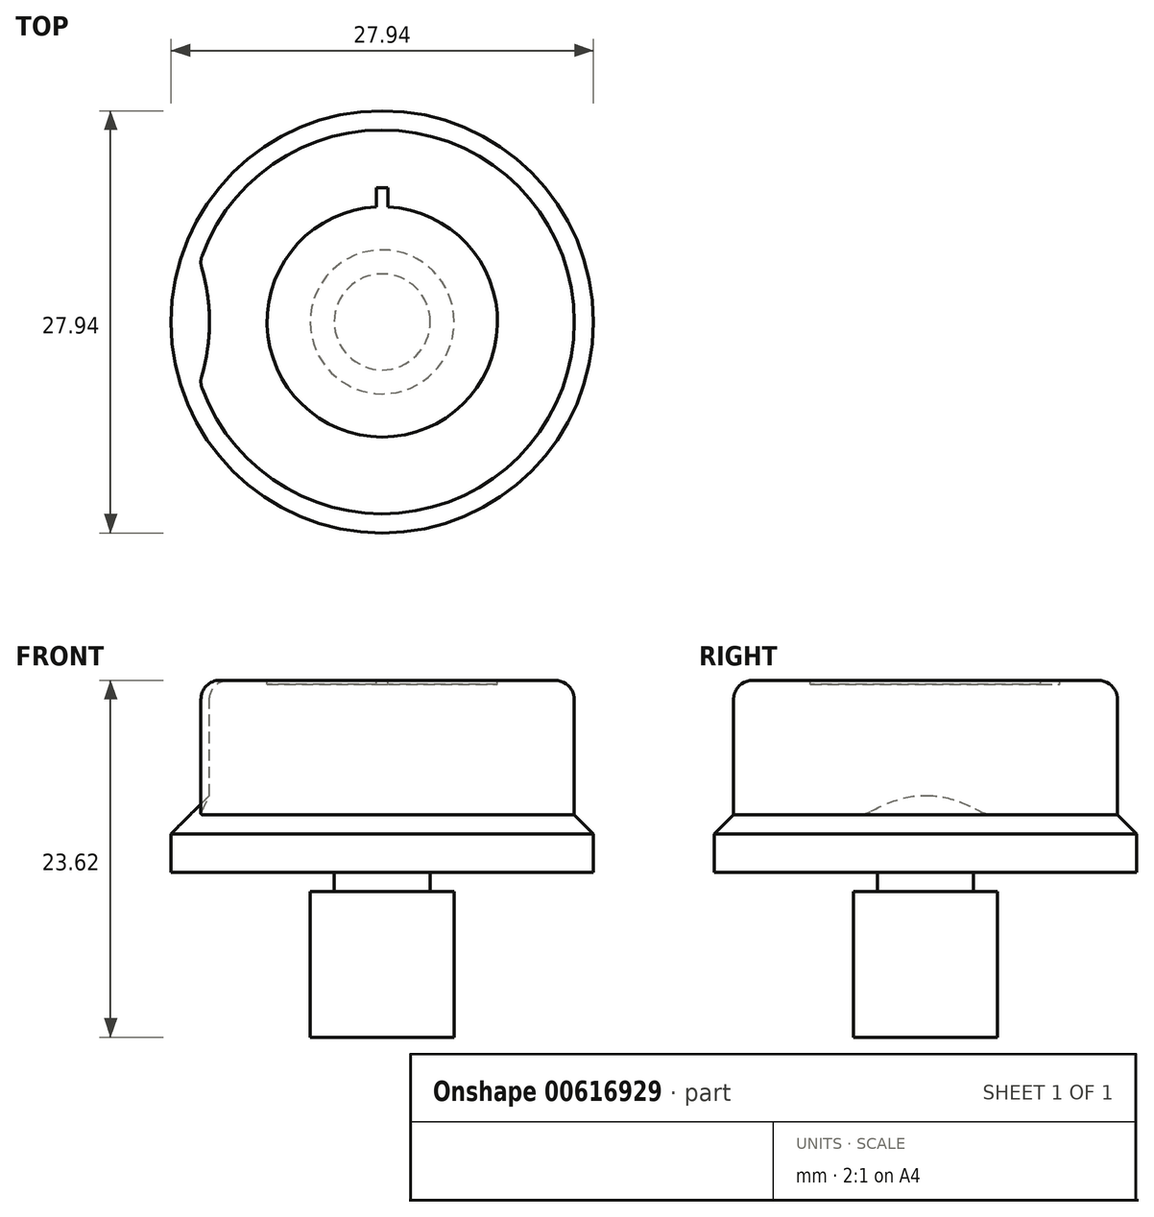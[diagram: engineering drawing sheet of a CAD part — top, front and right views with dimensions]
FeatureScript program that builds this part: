
annotation { "Feature Type Name" : "Feature", "Feature Type Description" : "" }
export const myFeature = defineFeature(function(context is Context, id is Id, definition is map)
    precondition{}
    {
        {
            var Q0;
            Q0=qCreatedBy(makeId("Front.planeOp"),FACE);
            var sketch = newSketch(context, id + "F0", { "sketchPlane" : qUnion([Q0])});
            skLineSegment(sketch, "E0", {"start": v(0, 0) * mm, "end": v(0, 23.62) * mm});
            skLineSegment(sketch, "E1", {"start": v(0, 23.62) * mm, "end": v(12.7, 23.62) * mm});
            skLineSegment(sketch, "E2", {"start": v(12.7, 23.62) * mm, "end": v(12.7, 14.73) * mm});
            skLineSegment(sketch, "E3", {"start": v(12.7, 14.73) * mm, "end": v(13.97, 13.46) * mm});
            skLineSegment(sketch, "E4", {"start": v(13.97, 13.46) * mm, "end": v(13.97, 10.92) * mm});
            skLineSegment(sketch, "E5", {"start": v(13.97, 10.92) * mm, "end": v(3.17, 10.92) * mm});
            skLineSegment(sketch, "E6", {"start": v(3.17, 10.92) * mm, "end": v(3.17, 9.65) * mm});
            skLineSegment(sketch, "E7", {"start": v(3.17, 9.65) * mm, "end": v(4.76, 9.65) * mm});
            skLineSegment(sketch, "E8", {"start": v(4.76, 9.65) * mm, "end": v(4.76, 0) * mm});
            skLineSegment(sketch, "E9", {"start": v(4.76, 0) * mm, "end": v(0, 0) * mm});
            skSolve(sketch);
        }
        {
            var Q0;
            Q0=makeQuery(id+"F0.imprint","IMPRINT",FACE,{"disambiguationData":[TD([[makeQuery(id+"F0.imprint","IMPRINT",EDGE,{"derivedFrom":sQuery(id+"F0.wireOp",EDGE,"E0")}),-1.0]])]});
            var Q1;
            Q1=sQuery(id+"F0.wireOp",EDGE,"E0");
            revolve(context, id + "F1", {"entities" : qUnion([Q0]), "axis" : qUnion([Q1]), "revolveType" : RevolveType.FULL});
        }
        {
            var Q0;
            Q0=makeQuery(id+"F1.opRevolve","SWEPT_FACE",FACE,{"disambiguationData":[OSD([sQuery(id+"F0.wireOp",EDGE,"E1")])]});
            var sketch = newSketch(context, id + "F2", { "sketchPlane" : qUnion([Q0])});
            skCircle(sketch, "E10", {"center": v(-24.13, 0) * mm, "radius": 12.7 * mm});
            skSolve(sketch);
        }
        {
            var Q0;
            Q0 = qSketchRegion(id + "F2", true);
            var Q1;
            Q1=makeQuery(id+"F1.opRevolve","SWEPT_FACE",FACE,{"disambiguationData":[OSD([sQuery(id+"F0.wireOp",EDGE,"E3")])]});
            extrude(context, id + "F3", {"entities" : qUnion([Q0]), "operationType" : NewBodyOperationType.REMOVE, "endBound" : BoundingType.UP_TO_SURFACE, "oppositeDirection" : true, "depth" : 25.4 * mm, "endBoundEntityFace" : qUnion([Q1]), "offsetDistance" : 25.4 * mm});
        }
        {
            var Q0;
            Q0=makeQuery(id+"F1.opRevolve","SWEPT_FACE",FACE,{"disambiguationData":[OSD([sQuery(id+"F0.wireOp",EDGE,"E1")])]});
            var Q1;
            {var subQ0=sQuery(id+"F2.wireOp",EDGE,"E10");var subQ4=makeQuery(id+"F3.boolean.opBoolean","COPY",FACE,{"derivedFrom":makeQuery(id+"F3.opExtrude","SWEPT_FACE",FACE,{"disambiguationData":[OSD([subQ0])]})});Q1=makeQuery(id+"FnJyQJZdkImbkAW_1.5.F3.boolean.opBoolean","INTERSECT",EDGE,{"disambiguationData":[OD(0.0)],"derivedFrom":[makeQuery(id+"FnJyQJZdkImbkAW_1.4.F3.boolean.opBoolean","SPLIT",FACE,{"disambiguationData":[TD([subQ4])],"derivedFrom":makeQuery(id+"FnJyQJZdkImbkAW_1.3.F3.boolean.opBoolean","SPLIT",FACE,{"disambiguationData":[TD([subQ4])],"derivedFrom":makeQuery(id+"FnJyQJZdkImbkAW_1.2.F3.boolean.opBoolean","SPLIT",FACE,{"disambiguationData":[TD([subQ4])],"derivedFrom":makeQuery(id+"FnJyQJZdkImbkAW_1.1.F3.boolean.opBoolean","SPLIT",FACE,{"disambiguationData":[OD(0.0)],"derivedFrom":makeQuery(id+"F1.opRevolve","SWEPT_FACE",FACE,{"disambiguationData":[OSD([sQuery(id+"F0.wireOp",EDGE,"E2")])]})})})})}),makeQuery(id+"FnJyQJZdkImbkAW_1.5.F3.opExtrude","SWEPT_FACE",FACE,{"disambiguationData":[OSD([subQ0])]})]});}
            var Q2;
            Q2=makeQuery(id+"F3.boolean.opBoolean","INTERSECT",EDGE,{"disambiguationData":[OD(0.0)],"derivedFrom":[makeQuery(id+"F1.opRevolve","SWEPT_FACE",FACE,{"disambiguationData":[OSD([sQuery(id+"F0.wireOp",EDGE,"E2")])]}),makeQuery(id+"F3.opExtrude","SWEPT_FACE",FACE,{"disambiguationData":[OSD([sQuery(id+"F2.wireOp",EDGE,"E10")])]})]});
            var Q3;
            Q3=makeQuery(id+"F3.boolean.opBoolean","INTERSECT",EDGE,{"disambiguationData":[OD(1.0)],"derivedFrom":[makeQuery(id+"F1.opRevolve","SWEPT_FACE",FACE,{"disambiguationData":[OSD([sQuery(id+"F0.wireOp",EDGE,"E2")])]}),makeQuery(id+"F3.opExtrude","SWEPT_FACE",FACE,{"disambiguationData":[OSD([sQuery(id+"F2.wireOp",EDGE,"E10")])]})]});
            var Q4;
            Q4=makeQuery(id+"FnJyQJZdkImbkAW_1.1.F3.boolean.opBoolean","INTERSECT",EDGE,{"disambiguationData":[OD(1.0)],"derivedFrom":[makeQuery(id+"F1.opRevolve","SWEPT_FACE",FACE,{"disambiguationData":[OSD([sQuery(id+"F0.wireOp",EDGE,"E2")])]}),makeQuery(id+"FnJyQJZdkImbkAW_1.1.F3.opExtrude","SWEPT_FACE",FACE,{"disambiguationData":[OSD([sQuery(id+"F2.wireOp",EDGE,"E10")])]})]});
            var Q5;
            Q5=makeQuery(id+"FnJyQJZdkImbkAW_1.1.F3.boolean.opBoolean","INTERSECT",EDGE,{"disambiguationData":[OD(0.0)],"derivedFrom":[makeQuery(id+"F1.opRevolve","SWEPT_FACE",FACE,{"disambiguationData":[OSD([sQuery(id+"F0.wireOp",EDGE,"E2")])]}),makeQuery(id+"FnJyQJZdkImbkAW_1.1.F3.opExtrude","SWEPT_FACE",FACE,{"disambiguationData":[OSD([sQuery(id+"F2.wireOp",EDGE,"E10")])]})]});
            var Q6;
            Q6=makeQuery(id+"FnJyQJZdkImbkAW_1.2.F3.boolean.opBoolean","INTERSECT",EDGE,{"disambiguationData":[OD(1.0)],"derivedFrom":[makeQuery(id+"FnJyQJZdkImbkAW_1.1.F3.boolean.opBoolean","SPLIT",FACE,{"disambiguationData":[OD(0.0)],"derivedFrom":makeQuery(id+"F1.opRevolve","SWEPT_FACE",FACE,{"disambiguationData":[OSD([sQuery(id+"F0.wireOp",EDGE,"E2")])]})}),makeQuery(id+"FnJyQJZdkImbkAW_1.2.F3.opExtrude","SWEPT_FACE",FACE,{"disambiguationData":[OSD([sQuery(id+"F2.wireOp",EDGE,"E10")])]})]});
            var Q7;
            Q7=makeQuery(id+"FnJyQJZdkImbkAW_1.2.F3.boolean.opBoolean","INTERSECT",EDGE,{"disambiguationData":[OD(0.0)],"derivedFrom":[makeQuery(id+"FnJyQJZdkImbkAW_1.1.F3.boolean.opBoolean","SPLIT",FACE,{"disambiguationData":[OD(0.0)],"derivedFrom":makeQuery(id+"F1.opRevolve","SWEPT_FACE",FACE,{"disambiguationData":[OSD([sQuery(id+"F0.wireOp",EDGE,"E2")])]})}),makeQuery(id+"FnJyQJZdkImbkAW_1.2.F3.opExtrude","SWEPT_FACE",FACE,{"disambiguationData":[OSD([sQuery(id+"F2.wireOp",EDGE,"E10")])]})]});
            var Q8;
            {var subQ0=sQuery(id+"F2.wireOp",EDGE,"E10");Q8=makeQuery(id+"FnJyQJZdkImbkAW_1.3.F3.boolean.opBoolean","INTERSECT",EDGE,{"disambiguationData":[OD(1.0)],"derivedFrom":[makeQuery(id+"FnJyQJZdkImbkAW_1.2.F3.boolean.opBoolean","SPLIT",FACE,{"disambiguationData":[TD([makeQuery(id+"F3.boolean.opBoolean","COPY",FACE,{"derivedFrom":makeQuery(id+"F3.opExtrude","SWEPT_FACE",FACE,{"disambiguationData":[OSD([subQ0])]})})])],"derivedFrom":makeQuery(id+"FnJyQJZdkImbkAW_1.1.F3.boolean.opBoolean","SPLIT",FACE,{"disambiguationData":[OD(0.0)],"derivedFrom":makeQuery(id+"F1.opRevolve","SWEPT_FACE",FACE,{"disambiguationData":[OSD([sQuery(id+"F0.wireOp",EDGE,"E2")])]})})}),makeQuery(id+"FnJyQJZdkImbkAW_1.3.F3.opExtrude","SWEPT_FACE",FACE,{"disambiguationData":[OSD([subQ0])]})]});}
            var Q9;
            {var subQ0=sQuery(id+"F2.wireOp",EDGE,"E10");Q9=makeQuery(id+"FnJyQJZdkImbkAW_1.3.F3.boolean.opBoolean","INTERSECT",EDGE,{"disambiguationData":[OD(0.0)],"derivedFrom":[makeQuery(id+"FnJyQJZdkImbkAW_1.2.F3.boolean.opBoolean","SPLIT",FACE,{"disambiguationData":[TD([makeQuery(id+"F3.boolean.opBoolean","COPY",FACE,{"derivedFrom":makeQuery(id+"F3.opExtrude","SWEPT_FACE",FACE,{"disambiguationData":[OSD([subQ0])]})})])],"derivedFrom":makeQuery(id+"FnJyQJZdkImbkAW_1.1.F3.boolean.opBoolean","SPLIT",FACE,{"disambiguationData":[OD(0.0)],"derivedFrom":makeQuery(id+"F1.opRevolve","SWEPT_FACE",FACE,{"disambiguationData":[OSD([sQuery(id+"F0.wireOp",EDGE,"E2")])]})})}),makeQuery(id+"FnJyQJZdkImbkAW_1.3.F3.opExtrude","SWEPT_FACE",FACE,{"disambiguationData":[OSD([subQ0])]})]});}
            var Q10;
            {var subQ0=sQuery(id+"F2.wireOp",EDGE,"E10");var subQ4=makeQuery(id+"F3.boolean.opBoolean","COPY",FACE,{"derivedFrom":makeQuery(id+"F3.opExtrude","SWEPT_FACE",FACE,{"disambiguationData":[OSD([subQ0])]})});Q10=makeQuery(id+"FnJyQJZdkImbkAW_1.4.F3.boolean.opBoolean","INTERSECT",EDGE,{"disambiguationData":[OD(1.0)],"derivedFrom":[makeQuery(id+"FnJyQJZdkImbkAW_1.3.F3.boolean.opBoolean","SPLIT",FACE,{"disambiguationData":[TD([subQ4])],"derivedFrom":makeQuery(id+"FnJyQJZdkImbkAW_1.2.F3.boolean.opBoolean","SPLIT",FACE,{"disambiguationData":[TD([subQ4])],"derivedFrom":makeQuery(id+"FnJyQJZdkImbkAW_1.1.F3.boolean.opBoolean","SPLIT",FACE,{"disambiguationData":[OD(0.0)],"derivedFrom":makeQuery(id+"F1.opRevolve","SWEPT_FACE",FACE,{"disambiguationData":[OSD([sQuery(id+"F0.wireOp",EDGE,"E2")])]})})})}),makeQuery(id+"FnJyQJZdkImbkAW_1.4.F3.opExtrude","SWEPT_FACE",FACE,{"disambiguationData":[OSD([subQ0])]})]});}
            var Q11;
            {var subQ0=sQuery(id+"F2.wireOp",EDGE,"E10");var subQ4=makeQuery(id+"F3.boolean.opBoolean","COPY",FACE,{"derivedFrom":makeQuery(id+"F3.opExtrude","SWEPT_FACE",FACE,{"disambiguationData":[OSD([subQ0])]})});Q11=makeQuery(id+"FnJyQJZdkImbkAW_1.4.F3.boolean.opBoolean","INTERSECT",EDGE,{"disambiguationData":[OD(0.0)],"derivedFrom":[makeQuery(id+"FnJyQJZdkImbkAW_1.3.F3.boolean.opBoolean","SPLIT",FACE,{"disambiguationData":[TD([subQ4])],"derivedFrom":makeQuery(id+"FnJyQJZdkImbkAW_1.2.F3.boolean.opBoolean","SPLIT",FACE,{"disambiguationData":[TD([subQ4])],"derivedFrom":makeQuery(id+"FnJyQJZdkImbkAW_1.1.F3.boolean.opBoolean","SPLIT",FACE,{"disambiguationData":[OD(0.0)],"derivedFrom":makeQuery(id+"F1.opRevolve","SWEPT_FACE",FACE,{"disambiguationData":[OSD([sQuery(id+"F0.wireOp",EDGE,"E2")])]})})})}),makeQuery(id+"FnJyQJZdkImbkAW_1.4.F3.opExtrude","SWEPT_FACE",FACE,{"disambiguationData":[OSD([subQ0])]})]});}
            var Q12;
            {var subQ0=sQuery(id+"F2.wireOp",EDGE,"E10");var subQ4=makeQuery(id+"F3.boolean.opBoolean","COPY",FACE,{"derivedFrom":makeQuery(id+"F3.opExtrude","SWEPT_FACE",FACE,{"disambiguationData":[OSD([subQ0])]})});Q12=makeQuery(id+"FnJyQJZdkImbkAW_1.5.F3.boolean.opBoolean","INTERSECT",EDGE,{"disambiguationData":[OD(1.0)],"derivedFrom":[makeQuery(id+"FnJyQJZdkImbkAW_1.4.F3.boolean.opBoolean","SPLIT",FACE,{"disambiguationData":[TD([subQ4])],"derivedFrom":makeQuery(id+"FnJyQJZdkImbkAW_1.3.F3.boolean.opBoolean","SPLIT",FACE,{"disambiguationData":[TD([subQ4])],"derivedFrom":makeQuery(id+"FnJyQJZdkImbkAW_1.2.F3.boolean.opBoolean","SPLIT",FACE,{"disambiguationData":[TD([subQ4])],"derivedFrom":makeQuery(id+"FnJyQJZdkImbkAW_1.1.F3.boolean.opBoolean","SPLIT",FACE,{"disambiguationData":[OD(0.0)],"derivedFrom":makeQuery(id+"F1.opRevolve","SWEPT_FACE",FACE,{"disambiguationData":[OSD([sQuery(id+"F0.wireOp",EDGE,"E2")])]})})})})}),makeQuery(id+"FnJyQJZdkImbkAW_1.5.F3.opExtrude","SWEPT_FACE",FACE,{"disambiguationData":[OSD([subQ0])]})]});}
            fillet(context, id + "F4", {"entities" : qUnion([Q0, Q1, Q2, Q3, Q4, Q5, Q6, Q7, Q8, Q9, Q10, Q11, Q12]), "radius" : 1.27 * mm, "tangentPropagation" : true, "allowEdgeOverflow" : false});
        }
        {
            var Q0;
            Q0=makeQuery(id+"F1.opRevolve","SWEPT_FACE",FACE,{"disambiguationData":[OSD([sQuery(id+"F0.wireOp",EDGE,"E1")])]});
            var sketch = newSketch(context, id + "F5", { "sketchPlane" : qUnion([Q0])});
            skCircle(sketch, "E11", {"center": v(0, 0) * mm, "radius": 7.62 * mm});
            skLineSegment(sketch, "E12.bottom", {"start": v(-0.38, 6.35) * mm, "end": v(0.38, 6.35) * mm});
            skLineSegment(sketch, "E12.top", {"start": v(-0.38, 8.9) * mm, "end": v(0.38, 8.9) * mm});
            skLineSegment(sketch, "E12.left", {"start": v(-0.38, 6.35) * mm, "end": v(-0.38, 8.9) * mm});
            skLineSegment(sketch, "E12.right", {"start": v(0.38, 6.35) * mm, "end": v(0.38, 8.9) * mm});
            skPoint(sketch, "E12.middle", {"position": v(0, 7.62) * mm});
            skSolve(sketch);
        }
        {
            var Q0;
            {var subQ5=sQuery(id+"F5.wireOp",EDGE,"E12.bottom");Q0=makeQuery(id+"F5.imprint","IMPRINT",FACE,{"disambiguationData":[TD([[makeQuery(id+"F5.imprint","IMPRINT",EDGE,{"derivedFrom":subQ5}),-1.0]])]});}
            var Q1;
            {var subQ5=sQuery(id+"F5.wireOp",EDGE,"E12.bottom");Q1=makeQuery(id+"F5.imprint","IMPRINT",FACE,{"disambiguationData":[TD([[makeQuery(id+"F5.imprint","IMPRINT",EDGE,{"derivedFrom":subQ5}),1.0]])]});}
            var Q2;
            {var subQ5=sQuery(id+"F5.wireOp",EDGE,"E12.top");Q2=makeQuery(id+"F5.imprint","IMPRINT",FACE,{"disambiguationData":[TD([[makeQuery(id+"F5.imprint","IMPRINT",EDGE,{"derivedFrom":subQ5}),-1.0]])]});}
            extrude(context, id + "F6", {"entities" : qUnion([Q0, Q1, Q2]), "operationType" : NewBodyOperationType.REMOVE, "oppositeDirection" : true, "depth" : 0.25 * mm, "offsetDistance" : 25.4 * mm});
        }
    });
